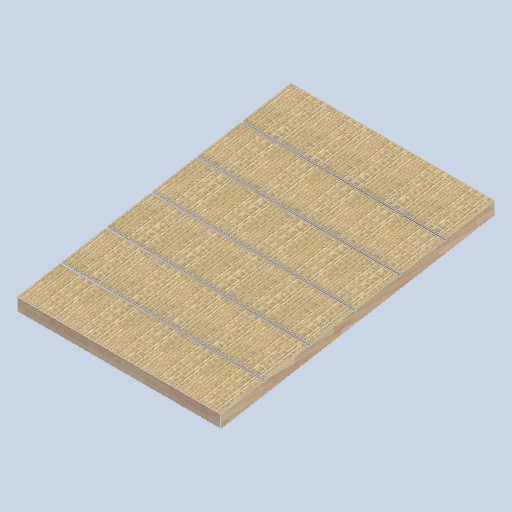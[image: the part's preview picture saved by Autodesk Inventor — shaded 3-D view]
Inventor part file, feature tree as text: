
AUTODESK INVENTOR PART (.ipt)
format: ipt  version: 2024.2 (Build 282272000, 272)  size: 325,632 bytes
history: native  units: in
note: dims shown in document units (in); Inventor stores cm internally (conversion verified against a paired STEP export)
features: sketch x5, other x3, plane x3
ambient origin geometry x8: Origin, YZ Plane, XZ Plane, XY Plane, X Axis, Y Axis, Z Axis, Center Point
bodies: Solid1 (feature_tree)
feature tree (11):
  other  "eave_panel_02_MIR.ipt"
  other  "Solid1::eave_panel_02_MIR.ipt"
  other  "TaggingFeature1"
  sketch  "Sketch1"  dims[d0=0.3937in]
  sketch  "Sketch2"
  sketch  "Sketch3"
  sketch  "Sketch4"
  sketch  "Sketch5"
  plane  "Work Plane1"
  plane  "Work Plane2"
  plane  "Work Plane3"
